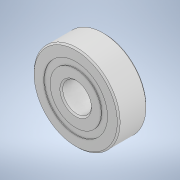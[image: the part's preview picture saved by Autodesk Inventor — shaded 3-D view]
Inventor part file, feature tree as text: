
AUTODESK INVENTOR PART (.ipt)
format: ipt  version: 2022 (Build 260153000, 153)  size: 560,640 bytes
history: mixed  units: in
note: dims shown in document units (in); Inventor stores cm internally (conversion verified against a paired STEP export)
features: other x11, revolve x5, imported_body x1
ambient origin geometry x8: Origin, YZ Plane, XZ Plane, XY Plane, X Axis, Y Axis, Z Axis, Center Point
bodies: Solid1 (imported_parasolid), Solid2 (imported_parasolid), Solid3 (imported_parasolid), Solid4 (imported_parasolid), Solid5 (imported_parasolid), Solid6 (imported_parasolid), Solid7 (imported_parasolid), Solid8 (imported_parasolid), Solid9 (imported_parasolid), Solid10 (imported_parasolid), Solid11 (imported_parasolid), Solid12 (imported_parasolid), Solid13 (imported_parasolid), Solid14 (imported_parasolid), Solid15 (imported_parasolid), Solid16 (imported_parasolid)
feature tree (17):
  revolve  "Revolve1"  [1 undecoded]
  revolve  "Revolve2"  [1 undecoded]
  revolve  "Revolve3"  [1 undecoded]
  other  "CirPattern1[1]"
  other  "CirPattern1[2]"
  other  "CirPattern1[3]"
  other  "CirPattern1[4]"
  other  "CirPattern1[5]"
  other  "CirPattern1[6]"
  other  "CirPattern1[7]"
  other  "CirPattern1[8]"
  other  "CirPattern1[9]"
  other  "CirPattern1[10]"
  other  "CirPattern1[11]"
  revolve  "Revolve5[1]"  [1 undecoded]
  revolve  "Revolve5[2]"  [1 undecoded]
  imported_body  NMx_Import_Brep_tag  [imported B-rep: ~36 faces, bbox_mm=[4.0, 0.0, 4.0]]
note: 5 required parameter values undecoded (feature->parameter linkage not recoverable at this tier; creation-order binding heuristic only, values carry confidence <= 0.55)
